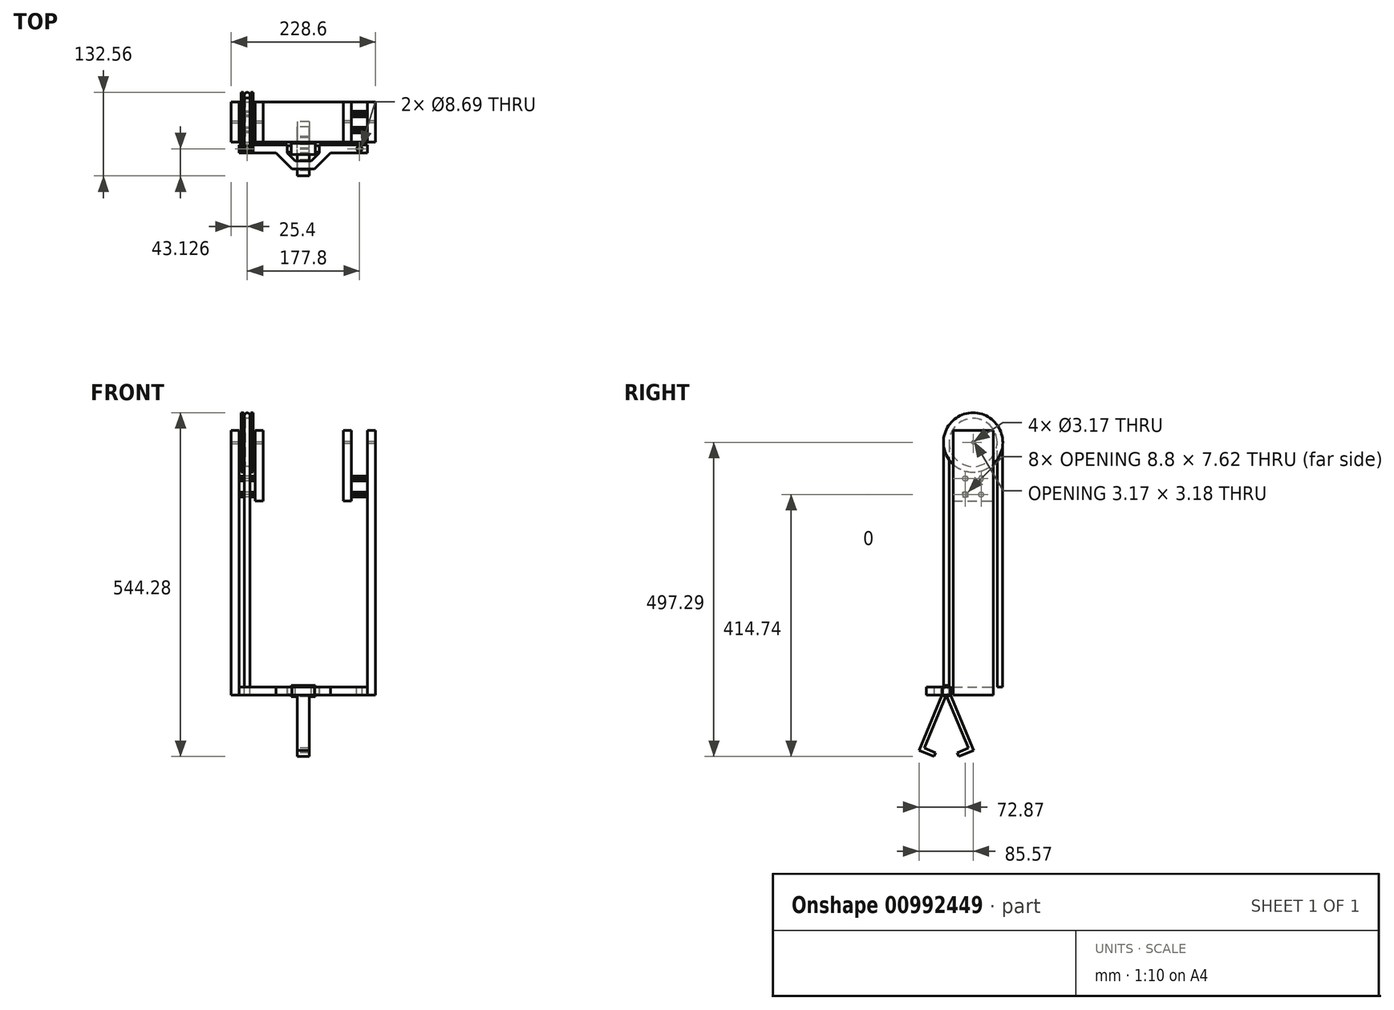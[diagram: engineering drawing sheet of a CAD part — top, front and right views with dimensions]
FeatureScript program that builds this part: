
annotation { "Feature Type Name" : "Feature", "Feature Type Description" : "" }
export const myFeature = defineFeature(function(context is Context, id is Id, definition is map)
    precondition{}
    {
        {
            var Q0;
            Q0=qCreatedBy(makeId("Front.planeOp"),FACE);
            var sketch = newSketch(context, id + "F0", { "sketchPlane" : qUnion([Q0])});
            skLineSegment(sketch, "E0", {"start": v(0, 0) * mm, "end": v(-114.3, 0) * mm});
            skLineSegment(sketch, "E1", {"start": v(-114.3, 0) * mm, "end": v(-114.3, 419.1) * mm});
            skLineSegment(sketch, "E2", {"start": v(-114.3, 419.1) * mm, "end": v(-101.6, 419.1) * mm});
            skLineSegment(sketch, "E3", {"start": v(-101.6, 419.1) * mm, "end": v(-101.6, 12.7) * mm});
            skLineSegment(sketch, "E4", {"start": v(-101.6, 12.7) * mm, "end": v(0, 12.7) * mm});
            skLineSegment(sketch, "E5", {"start": v(0, 12.7) * mm, "end": v(0, 0) * mm});
            skSolve(sketch);
        }
        {
            var Q0;
            Q0=makeQuery(id+"F0.imprint","IMPRINT",FACE,{"disambiguationData":[TD([[makeQuery(id+"F0.imprint","IMPRINT",EDGE,{"derivedFrom":sQuery(id+"F0.wireOp",EDGE,"E0")}),-1.0]])]});
            extrude(context, id + "F1", {"entities" : qUnion([Q0]), "endBound" : BoundingType.SYMMETRIC, "depth" : 63.5 * mm, "offsetDistance" : 25.4 * mm});
        }
        {
            var Q0;
            Q0=makeQuery(id+"F1.opExtrude","SWEPT_FACE",FACE,{"disambiguationData":[OSD([sQuery(id+"F0.wireOp",EDGE,"E3")])]});
            var sketch = newSketch(context, id + "F2", { "sketchPlane" : qUnion([Q0])});
            skCircle(sketch, "E6.cCircle", {"center": v(-12.7, 342.9) * mm, "radius": 3.81 * mm, "construction": true});
            skLineSegment(sketch, "E6.0", {"start": v(-10.5, 339.1) * mm, "end": v(-14.9, 339.1) * mm});
            skLineSegment(sketch, "E6.1", {"start": v(-14.9, 339.1) * mm, "end": v(-17.1, 342.9) * mm});
            skLineSegment(sketch, "E6.2", {"start": v(-17.1, 342.9) * mm, "end": v(-14.9, 346.71) * mm});
            skLineSegment(sketch, "E6.3", {"start": v(-14.9, 346.71) * mm, "end": v(-10.5, 346.71) * mm});
            skLineSegment(sketch, "E6.4", {"start": v(-10.5, 346.71) * mm, "end": v(-8.3, 342.9) * mm});
            skLineSegment(sketch, "E6.5", {"start": v(-8.3, 342.9) * mm, "end": v(-10.5, 339.1) * mm});
            skPoint(sketch, "E6.0.midPoint", {"position": v(-12.7, 339.1) * mm});
            skLineSegment(sketch, "E7.MirrorCS", {"start": v(17.1, 342.9) * mm, "end": v(14.9, 346.71) * mm});
            skLineSegment(sketch, "E8.MirrorCS", {"start": v(10.5, 339.1) * mm, "end": v(14.9, 339.1) * mm});
            skLineSegment(sketch, "E9.MirrorCS", {"start": v(14.9, 346.71) * mm, "end": v(10.5, 346.71) * mm});
            skLineSegment(sketch, "E10.MirrorCS", {"start": v(8.3, 342.9) * mm, "end": v(10.5, 339.1) * mm});
            skPoint(sketch, "E11.MirrorP", {"position": v(12.7, 339.1) * mm});
            skLineSegment(sketch, "E12.MirrorCS", {"start": v(10.5, 346.71) * mm, "end": v(8.3, 342.9) * mm});
            skLineSegment(sketch, "E13.MirrorCS", {"start": v(14.9, 339.1) * mm, "end": v(17.1, 342.9) * mm});
            skCircle(sketch, "E14.MirrorC", {"center": v(12.7, 342.9) * mm, "radius": 3.81 * mm, "construction": true});
            skLineSegment(sketch, "E15", {"start": v(-31.75, 330.2) * mm, "end": v(31.75, 330.2) * mm, "construction": true});
            skLineSegment(sketch, "E16.MirrorCS", {"start": v(-10.5, 313.7) * mm, "end": v(-8.3, 317.5) * mm});
            skLineSegment(sketch, "E17.MirrorCS", {"start": v(17.1, 317.5) * mm, "end": v(14.9, 313.69) * mm});
            skLineSegment(sketch, "E18.MirrorCS", {"start": v(-14.9, 313.7) * mm, "end": v(-10.5, 313.7) * mm});
            skLineSegment(sketch, "E19.MirrorCS", {"start": v(-10.5, 321.3) * mm, "end": v(-14.9, 321.3) * mm});
            skLineSegment(sketch, "E20.MirrorCS", {"start": v(8.3, 317.5) * mm, "end": v(10.5, 321.3) * mm});
            skLineSegment(sketch, "E21.MirrorCS", {"start": v(14.9, 321.31) * mm, "end": v(17.1, 317.5) * mm});
            skLineSegment(sketch, "E22.MirrorCS", {"start": v(-17.1, 317.5) * mm, "end": v(-14.9, 313.7) * mm});
            skLineSegment(sketch, "E23.MirrorCS", {"start": v(-14.9, 321.3) * mm, "end": v(-17.1, 317.5) * mm});
            skCircle(sketch, "E24.MirrorC", {"center": v(-12.7, 317.5) * mm, "radius": 3.81 * mm, "construction": true});
            skLineSegment(sketch, "E25.MirrorCS", {"start": v(10.5, 313.7) * mm, "end": v(8.3, 317.5) * mm});
            skCircle(sketch, "E26.MirrorC", {"center": v(12.7, 317.5) * mm, "radius": 3.81 * mm, "construction": true});
            skLineSegment(sketch, "E27.MirrorCS", {"start": v(10.5, 321.3) * mm, "end": v(14.9, 321.3) * mm});
            skLineSegment(sketch, "E28.MirrorCS", {"start": v(14.9, 313.7) * mm, "end": v(10.5, 313.7) * mm});
            skLineSegment(sketch, "E29.MirrorCS", {"start": v(-8.3, 317.5) * mm, "end": v(-10.5, 321.3) * mm});
            skPoint(sketch, "E30.MirrorP", {"position": v(-12.7, 321.3) * mm});
            skPoint(sketch, "E31.MirrorP", {"position": v(12.7, 321.3) * mm});
            skSolve(sketch);
        }
        {
            var Q0;
            Q0 = qSketchRegion(id + "F2", true);
            extrude(context, id + "F3", {"entities" : qUnion([Q0]), "operationType" : NewBodyOperationType.ADD, "depth" : 25.4 * mm, "offsetDistance" : 25.4 * mm});
        }
        {
            var Q0;
            Q0=makeQuery(id+"F3.opExtrude","CAP_FACE",FACE,{"disambiguationData":[OSD([sQuery(id+"F2.wireOp",EDGE,"E7.MirrorCS"),sQuery(id+"F2.wireOp",EDGE,"E8.MirrorCS"),sQuery(id+"F2.wireOp",EDGE,"E9.MirrorCS"),sQuery(id+"F2.wireOp",EDGE,"E10.MirrorCS"),sQuery(id+"F2.wireOp",EDGE,"E12.MirrorCS"),sQuery(id+"F2.wireOp",EDGE,"E13.MirrorCS")])],"isStart":false});
            var sketch = newSketch(context, id + "F4", { "sketchPlane" : qUnion([Q0])});
            skLineSegment(sketch, "E32.0", {"start": v(-31.75, 419.1) * mm, "end": v(31.75, 419.1) * mm});
            skLineSegment(sketch, "E33.0.0", {"start": v(-8.3, 317.5) * mm, "end": v(-10.5, 321.3) * mm, "construction": true});
            skLineSegment(sketch, "E33.0.1", {"start": v(-10.5, 321.3) * mm, "end": v(-14.9, 321.3) * mm, "construction": true});
            skLineSegment(sketch, "E33.0.2", {"start": v(-14.9, 321.3) * mm, "end": v(-17.1, 317.5) * mm, "construction": true});
            skLineSegment(sketch, "E33.0.3", {"start": v(-17.1, 317.5) * mm, "end": v(-14.9, 313.7) * mm, "construction": true});
            skLineSegment(sketch, "E33.0.4", {"start": v(-14.9, 313.7) * mm, "end": v(-10.5, 313.7) * mm, "construction": true});
            skLineSegment(sketch, "E33.0.5", {"start": v(-10.5, 313.7) * mm, "end": v(-8.3, 317.5) * mm, "construction": true});
            skLineSegment(sketch, "E34.0.0", {"start": v(8.3, 317.5) * mm, "end": v(10.5, 313.7) * mm, "construction": true});
            skLineSegment(sketch, "E34.0.1", {"start": v(10.5, 313.7) * mm, "end": v(14.9, 313.7) * mm, "construction": true});
            skLineSegment(sketch, "E34.0.2", {"start": v(14.9, 313.69) * mm, "end": v(17.1, 317.5) * mm, "construction": true});
            skLineSegment(sketch, "E34.0.3", {"start": v(17.1, 317.5) * mm, "end": v(14.9, 321.31) * mm, "construction": true});
            skLineSegment(sketch, "E34.0.4", {"start": v(14.9, 321.3) * mm, "end": v(10.5, 321.3) * mm, "construction": true});
            skLineSegment(sketch, "E34.0.5", {"start": v(10.5, 321.3) * mm, "end": v(8.3, 317.5) * mm, "construction": true});
            skLineSegment(sketch, "E35.0", {"start": v(-31.75, 419.1) * mm, "end": v(-31.75, 12.7) * mm, "construction": true});
            skLineSegment(sketch, "E36.0", {"start": v(31.75, 419.1) * mm, "end": v(31.75, 12.7) * mm, "construction": true});
            skLineSegment(sketch, "E37", {"start": v(-31.75, 419.1) * mm, "end": v(-31.75, 307.34) * mm});
            skLineSegment(sketch, "E38", {"start": v(-31.75, 307.34) * mm, "end": v(31.75, 307.34) * mm});
            skLineSegment(sketch, "E39", {"start": v(31.75, 307.34) * mm, "end": v(31.75, 419.1) * mm});
            skSolve(sketch);
        }
        {
            var Q0;
            Q0 = qSketchRegion(id + "F4", true);
            extrude(context, id + "F5", {"entities" : qUnion([Q0]), "operationType" : NewBodyOperationType.ADD, "depth" : 12.7 * mm, "offsetDistance" : 25.4 * mm});
        }
        {
            var Q0;
            Q0=makeQuery(id+"F5.opExtrude","CAP_FACE",FACE,{"disambiguationData":[OSD([sQuery(id+"F4.wireOp",EDGE,"E32.0"),sQuery(id+"F4.wireOp",EDGE,"E37"),sQuery(id+"F4.wireOp",EDGE,"E38"),sQuery(id+"F4.wireOp",EDGE,"E39")])],"isStart":false});
            var sketch = newSketch(context, id + "F6", { "sketchPlane" : qUnion([Q0])});
            skCircle(sketch, "E40", {"center": v(0, 400.05) * mm, "radius": 1.59 * mm});
            skSolve(sketch);
        }
        {
            var Q0;
            Q0 = qSketchRegion(id + "F6", true);
            extrude(context, id + "F7", {"entities" : qUnion([Q0]), "operationType" : NewBodyOperationType.REMOVE, "endBound" : BoundingType.THROUGH_ALL, "oppositeDirection" : true, "depth" : 25.4 * mm, "offsetDistance" : 25.4 * mm});
        }
        {
            var Q0;
            Q0=makeQuery(id+"F1.opExtrude","SWEPT_BODY",BODY,{"disambiguationData":[OSD([sQuery(id+"F0.wireOp",EDGE,"E0"),sQuery(id+"F0.wireOp",EDGE,"E1"),sQuery(id+"F0.wireOp",EDGE,"E2"),sQuery(id+"F0.wireOp",EDGE,"E3"),sQuery(id+"F0.wireOp",EDGE,"E4"),sQuery(id+"F0.wireOp",EDGE,"E5")])]});
            var Q1;
            Q1=qCreatedBy(makeId("Right.planeOp"),FACE);
            mirror(context, id + "F8", {"operationType" : NewBodyOperationType.ADD, "entities" : qUnion([Q0]), "mirrorPlane" : qUnion([Q1])});
        }
        {
            var Q0;
            Q0=qCreatedBy(makeId("Front.planeOp"),FACE);
            var sketch = newSketch(context, id + "F9", { "sketchPlane" : qUnion([Q0])});
            skLineSegment(sketch, "E41", {"start": v(-101.6, 398.46) * mm, "end": v(-114.3, 398.46) * mm, "construction": true});
            skLineSegment(sketch, "E42", {"start": v(-114.3, 401.64) * mm, "end": v(-101.6, 401.64) * mm, "construction": true});
            skLineSegment(sketch, "E43.0", {"start": v(-114.3, 398.46) * mm, "end": v(-114.3, 401.64) * mm, "construction": true});
            skLineSegment(sketch, "E44", {"start": v(-114.3, 400.05) * mm, "end": v(-63.5, 400.05) * mm, "construction": true});
            skLineSegment(sketch, "E45.0", {"start": v(-63.5, 401.64) * mm, "end": v(-63.5, 398.46) * mm, "construction": true});
            skLineSegment(sketch, "E46.0", {"start": v(-101.6, 419.1) * mm, "end": v(-101.6, 12.7) * mm, "construction": true});
            skLineSegment(sketch, "E47.0", {"start": v(-76.2, 419.1) * mm, "end": v(-76.2, 307.34) * mm, "construction": true});
            skLineSegment(sketch, "E48", {"start": v(-98.43, 400.05) * mm, "end": v(-98.43, 447.04) * mm});
            skLineSegment(sketch, "E49", {"start": v(-98.43, 447.04) * mm, "end": v(-94.62, 447.04) * mm});
            skLineSegment(sketch, "E50", {"start": v(-94.62, 447.04) * mm, "end": v(-92.23, 438.15) * mm});
            skLineSegment(sketch, "E51", {"start": v(-92.23, 438.15) * mm, "end": v(-85.57, 438.15) * mm});
            skLineSegment(sketch, "E52", {"start": v(-85.57, 438.15) * mm, "end": v(-83.18, 447.04) * mm});
            skLineSegment(sketch, "E53", {"start": v(-83.19, 447.04) * mm, "end": v(-79.38, 447.04) * mm});
            skLineSegment(sketch, "E54", {"start": v(-79.38, 447.04) * mm, "end": v(-79.38, 400.05) * mm});
            skLineSegment(sketch, "E55", {"start": v(-79.38, 400.05) * mm, "end": v(-98.43, 400.05) * mm});
            skLineSegment(sketch, "E56", {"start": v(-76.2, 419.1) * mm, "end": v(-101.6, 419.1) * mm, "construction": true});
            skLineSegment(sketch, "E57", {"start": v(-88.9, 419.1) * mm, "end": v(-88.9, 400.05) * mm, "construction": true});
            skSolve(sketch);
        }
        {
            var Q0;
            Q0=makeQuery(id+"F9.imprint","IMPRINT",FACE,{"disambiguationData":[TD([[makeQuery(id+"F9.imprint","IMPRINT",EDGE,{"derivedFrom":sQuery(id+"F9.wireOp",EDGE,"E48")}),-1.0]])]});
            var Q1;
            Q1=sQuery(id+"F9.wireOp",EDGE,"E44");
            revolve(context, id + "F10", {"surfaceOperationType" : NewSurfaceOperationType.NEW, "entities" : qUnion([Q0]), "axis" : qUnion([Q1]), "revolveType" : RevolveType.FULL});
        }
        {
            var Q0;
            Q0=qCreatedBy(makeId("Front.planeOp"),FACE);
            var sketch = newSketch(context, id + "F11", { "sketchPlane" : qUnion([Q0])});
            skLineSegment(sketch, "E58", {"start": v(-93.23, 441.87) * mm, "end": v(-92.22, 438.11) * mm, "construction": true});
            skLineSegment(sketch, "E59", {"start": v(-92.08, 438.15) * mm, "end": v(-85.73, 438.15) * mm, "construction": true});
            skLineSegment(sketch, "E60", {"start": v(-85.58, 438.11) * mm, "end": v(-84.57, 441.87) * mm, "construction": true});
            skCircle(sketch, "E61", {"center": v(-88.9, 442.5) * mm, "radius": 4.34 * mm});
            skSolve(sketch);
        }
        {
            var Q0;
            Q0=qCreatedBy(makeId("Right.planeOp"),FACE);
            var sketch = newSketch(context, id + "F12", { "sketchPlane" : qUnion([Q0])});
            skLineSegment(sketch, "E62.0", {"start": v(0, 438.15) * mm, "end": v(0, 446.84) * mm, "construction": true});
            skPoint(sketch, "E63.0", {"position": v(0, 442.5) * mm});
            skCircle(sketch, "E64.0.0", {"center": v(0, 400.05) * mm, "radius": 47 * mm, "construction": true});
            skLineSegment(sketch, "E65.0.1", {"start": v(31.75, 12.7) * mm, "end": v(-31.75, 12.7) * mm, "construction": true});
            skLineSegment(sketch, "E65.0.3", {"start": v(-31.75, 12.7) * mm, "end": v(31.75, 12.7) * mm, "construction": true});
            skArc(sketch, "E66", {"start": v(0, 442.5) * mm, "mid": v(-30.01, 430.06) * mm, "end": v(-42.44, 400.05) * mm});
            skArc(sketch, "E67", {"start": v(0, 442.5) * mm, "mid": v(30.01, 430.06) * mm, "end": v(42.44, 400.05) * mm});
            skLineSegment(sketch, "E68", {"start": v(-42.44, 400.05) * mm, "end": v(-42.44, 12.7) * mm});
            skLineSegment(sketch, "E69", {"start": v(42.44, 400.05) * mm, "end": v(42.44, 12.7) * mm});
            skSolve(sketch);
        }
        {
            var Q0;
            Q0=makeQuery(id+"F11.imprint","IMPRINT",FACE,{"disambiguationData":[TD([[makeQuery(id+"F11.imprint","IMPRINT",EDGE,{"derivedFrom":sQuery(id+"F11.wireOp",EDGE,"E61")}),1.0]])]});
            var Q1;
            Q1=sQuery(id+"F12.wireOp",EDGE,"E69");
            var Q2;
            Q2=sQuery(id+"F12.wireOp",EDGE,"E67");
            var Q3;
            Q3=sQuery(id+"F12.wireOp",EDGE,"E66");
            var Q4;
            Q4=sQuery(id+"F12.wireOp",EDGE,"E68");
            sweep(context, id + "F13", {"profiles" : qUnion([Q0]), "path" : qUnion([Q1, Q2, Q3, Q4])});
        }
        {
            var Q0;
            Q0=makeQuery(id+"F13.opSweep","CAP_FACE",FACE,{"disambiguationData":[OSD([sQuery(id+"F11.wireOp",EDGE,"E61"),sQuery(id+"F12.wireOp",VERTEX,"E68.end")])],"isStart":false});
            var sketch = newSketch(context, id + "F14", { "sketchPlane" : qUnion([Q0])});
            skCircle(sketch, "E70.0.0", {"center": v(-88.9, 42.44) * mm, "radius": 4.34 * mm, "construction": true});
            skLineSegment(sketch, "E71", {"start": v(-88.9, 42.44) * mm, "end": v(0, 42.44) * mm, "construction": true});
            skLineSegment(sketch, "E72.bottom", {"start": v(-101.6, 48.8) * mm, "end": v(101.6, 48.8) * mm, "construction": true});
            skLineSegment(sketch, "E72.top", {"start": v(-101.6, 36.1) * mm, "end": v(101.6, 36.1) * mm, "construction": true});
            skLineSegment(sketch, "E72.left", {"start": v(-101.6, 48.8) * mm, "end": v(-101.6, 36.1) * mm});
            skLineSegment(sketch, "E72.right", {"start": v(101.6, 48.8) * mm, "end": v(101.6, 36.1) * mm});
            skLineSegment(sketch, "E73", {"start": v(-43.18, 48.8) * mm, "end": v(-17.78, 74.2) * mm});
            skLineSegment(sketch, "E74", {"start": v(-17.78, 74.2) * mm, "end": v(17.78, 74.2) * mm});
            skLineSegment(sketch, "E75", {"start": v(17.78, 74.2) * mm, "end": v(43.18, 48.8) * mm});
            skLineSegment(sketch, "E76", {"start": v(43.18, 48.8) * mm, "end": v(101.6, 48.8) * mm});
            skLineSegment(sketch, "E77", {"start": v(-43.18, 48.8) * mm, "end": v(-101.6, 48.8) * mm});
            skLineSegment(sketch, "E78.top", {"start": v(-12.7, 61.5) * mm, "end": v(12.7, 61.5) * mm});
            skLineSegment(sketch, "E78.left", {"start": v(-25.4, 48.8) * mm, "end": v(-12.7, 61.5) * mm});
            skLineSegment(sketch, "E78.right", {"start": v(25.4, 48.8) * mm, "end": v(12.7, 61.5) * mm});
            skLineSegment(sketch, "E79", {"start": v(-25.4, 48.8) * mm, "end": v(-25.4, 36.1) * mm});
            skLineSegment(sketch, "E80", {"start": v(25.4, 48.8) * mm, "end": v(25.4, 36.1) * mm});
            skLineSegment(sketch, "E81", {"start": v(-101.6, 36.1) * mm, "end": v(-25.4, 36.1) * mm});
            skLineSegment(sketch, "E82", {"start": v(25.4, 36.1) * mm, "end": v(101.6, 36.1) * mm});
            skSolve(sketch);
        }
        {
            var Q0;
            Q0 = qSketchRegion(id + "F14", true);
            extrude(context, id + "F15", {"entities" : qUnion([Q0]), "depth" : 12.7 * mm, "offsetDistance" : 25.4 * mm});
        }
        {
            var Q0;
            Q0=makeQuery(id+"F15.opExtrude","CAP_EDGE",EDGE,{"disambiguationData":[OSD([sQuery(id+"F14.wireOp",EDGE,"E79")])],"isStart":true});
            cPoint(context, id + "F16", {"entities" : qUnion([Q0]), "parameter" : 0.5});
        }
        {
            var Q0;
            Q0=qCreatedBy(makeId("Front.planeOp"),FACE);
            var Q1;
            Q1 = qCreatedBy(id + "F16" ,VERTEX);
            cPlane(context, id + "F17", {"entities" : qUnion([Q0, Q1]), "cplaneType" : CPlaneType.PLANE_POINT, "offset" : 25.4 * mm, "width" : 152.4 * mm, "height" : 152.4 * mm});
        }
        {
            var Q0;
            Q0=qCreatedBy(id+"F17.planeOp",FACE);
            var sketch = newSketch(context, id + "F18", { "sketchPlane" : qUnion([Q0])});
            skLineSegment(sketch, "E83", {"start": v(-25.4, 0) * mm, "end": v(-25.4, 12.7) * mm, "construction": true});
            skLineSegment(sketch, "E84", {"start": v(25.4, 0) * mm, "end": v(25.4, 12.7) * mm, "construction": true});
            skLineSegment(sketch, "E85", {"start": v(-25.4, 6.35) * mm, "end": v(25.4, 6.35) * mm});
            skLineSegment(sketch, "E86", {"start": v(-25.4, 6.35) * mm, "end": v(-25.4, 11.43) * mm});
            skLineSegment(sketch, "E87", {"start": v(-25.4, 11.43) * mm, "end": v(-19.05, 11.43) * mm});
            skLineSegment(sketch, "E88", {"start": v(-19.05, 11.43) * mm, "end": v(-19.05, 15.24) * mm});
            skLineSegment(sketch, "E89", {"start": v(-19.05, 15.24) * mm, "end": v(19.05, 15.24) * mm});
            skLineSegment(sketch, "E90", {"start": v(19.05, 15.24) * mm, "end": v(19.05, 11.43) * mm});
            skLineSegment(sketch, "E91", {"start": v(19.05, 11.43) * mm, "end": v(25.4, 11.43) * mm});
            skLineSegment(sketch, "E92", {"start": v(25.4, 11.43) * mm, "end": v(25.4, 6.35) * mm});
            skSolve(sketch);
        }
        {
            var Q0;
            Q0=makeQuery(id+"F18.imprint","IMPRINT",FACE,{"disambiguationData":[TD([[makeQuery(id+"F18.imprint","IMPRINT",EDGE,{"derivedFrom":sQuery(id+"F18.wireOp",EDGE,"E85")}),1.0]])]});
            var Q1;
            Q1=sQuery(id+"F18.wireOp",EDGE,"E85");
            revolve(context, id + "F19", {"surfaceOperationType" : NewSurfaceOperationType.NEW, "entities" : qUnion([Q0]), "axis" : qUnion([Q1]), "revolveType" : RevolveType.FULL});
        }
        {
            var Q0;
            Q0=qCreatedBy(makeId("Right.planeOp"),FACE);
            var sketch = newSketch(context, id + "F20", { "sketchPlane" : qUnion([Q0])});
            skCircle(sketch, "E93.0", {"center": v(-42.44, 6.35) * mm, "radius": 8.9 * mm, "construction": true});
            skLineSegment(sketch, "E94", {"start": v(-46.69, 6.35) * mm, "end": v(-85.57, -87.52) * mm});
            skLineSegment(sketch, "E95", {"start": v(-85.57, -87.52) * mm, "end": v(-62.1, -97.24) * mm});
            skLineSegment(sketch, "E96", {"start": v(-62.1, -97.24) * mm, "end": v(-59.67, -91.37) * mm});
            skLineSegment(sketch, "E97", {"start": v(-59.67, -91.37) * mm, "end": v(-77.27, -84.08) * mm});
            skLineSegment(sketch, "E98", {"start": v(-77.27, -84.08) * mm, "end": v(-42.44, 0) * mm});
            skLineSegment(sketch, "E99", {"start": v(-42.44, 0) * mm, "end": v(-7.62, -84.08) * mm});
            skLineSegment(sketch, "E100", {"start": v(-7.62, -84.08) * mm, "end": v(-25.22, -91.37) * mm});
            skLineSegment(sketch, "E101", {"start": v(-25.22, -91.37) * mm, "end": v(-22.79, -97.24) * mm});
            skLineSegment(sketch, "E102", {"start": v(-22.79, -97.24) * mm, "end": v(0.68, -87.52) * mm});
            skLineSegment(sketch, "E103", {"start": v(0.68, -87.52) * mm, "end": v(-38.2, 6.35) * mm});
            skLineSegment(sketch, "E104", {"start": v(-38.2, 6.35) * mm, "end": v(-46.69, 6.35) * mm});
            skLineSegment(sketch, "E105", {"start": v(-77.27, -84.08) * mm, "end": v(-83.14, -81.65) * mm, "construction": true});
            skLineSegment(sketch, "E106", {"start": v(-42.44, 0) * mm, "end": v(-42.44, 6.35) * mm, "construction": true});
            skSolve(sketch);
        }
        {
            var Q0;
            Q0 = qSketchRegion(id + "F20", true);
            extrude(context, id + "F21", {"entities" : qUnion([Q0]), "operationType" : NewBodyOperationType.ADD, "endBound" : BoundingType.SYMMETRIC, "depth" : 19.05 * mm, "offsetDistance" : 25.4 * mm});
        }
        {
            var Q0;
            Q0=makeQuery(id+"F15.opExtrude","CAP_FACE",FACE,{"disambiguationData":[OSD([sQuery(id+"F14.wireOp",EDGE,"E72.left"),sQuery(id+"F14.wireOp",EDGE,"E72.right"),sQuery(id+"F14.wireOp",EDGE,"E73"),sQuery(id+"F14.wireOp",EDGE,"E74"),sQuery(id+"F14.wireOp",EDGE,"E75"),sQuery(id+"F14.wireOp",EDGE,"E76"),sQuery(id+"F14.wireOp",EDGE,"E77"),sQuery(id+"F14.wireOp",EDGE,"E78.top"),sQuery(id+"F14.wireOp",EDGE,"E78.left"),sQuery(id+"F14.wireOp",EDGE,"E78.right"),sQuery(id+"F14.wireOp",EDGE,"E79"),sQuery(id+"F14.wireOp",EDGE,"E80"),sQuery(id+"F14.wireOp",EDGE,"E81"),sQuery(id+"F14.wireOp",EDGE,"E82")])],"isStart":true});
            var sketch = newSketch(context, id + "F22", { "sketchPlane" : qUnion([Q0])});
            skCircle(sketch, "E107.0", {"center": v(-88.9, -42.44) * mm, "radius": 4.34 * mm});
            skCircle(sketch, "E108.MirrorC", {"center": v(88.9, -42.44) * mm, "radius": 4.34 * mm});
            skSolve(sketch);
        }
        {
            var Q0;
            Q0 = qSketchRegion(id + "F22", true);
            extrude(context, id + "F23", {"entities" : qUnion([Q0]), "operationType" : NewBodyOperationType.REMOVE, "endBound" : BoundingType.THROUGH_ALL, "oppositeDirection" : true, "depth" : 25.4 * mm, "offsetDistance" : 25.4 * mm});
        }
    });
